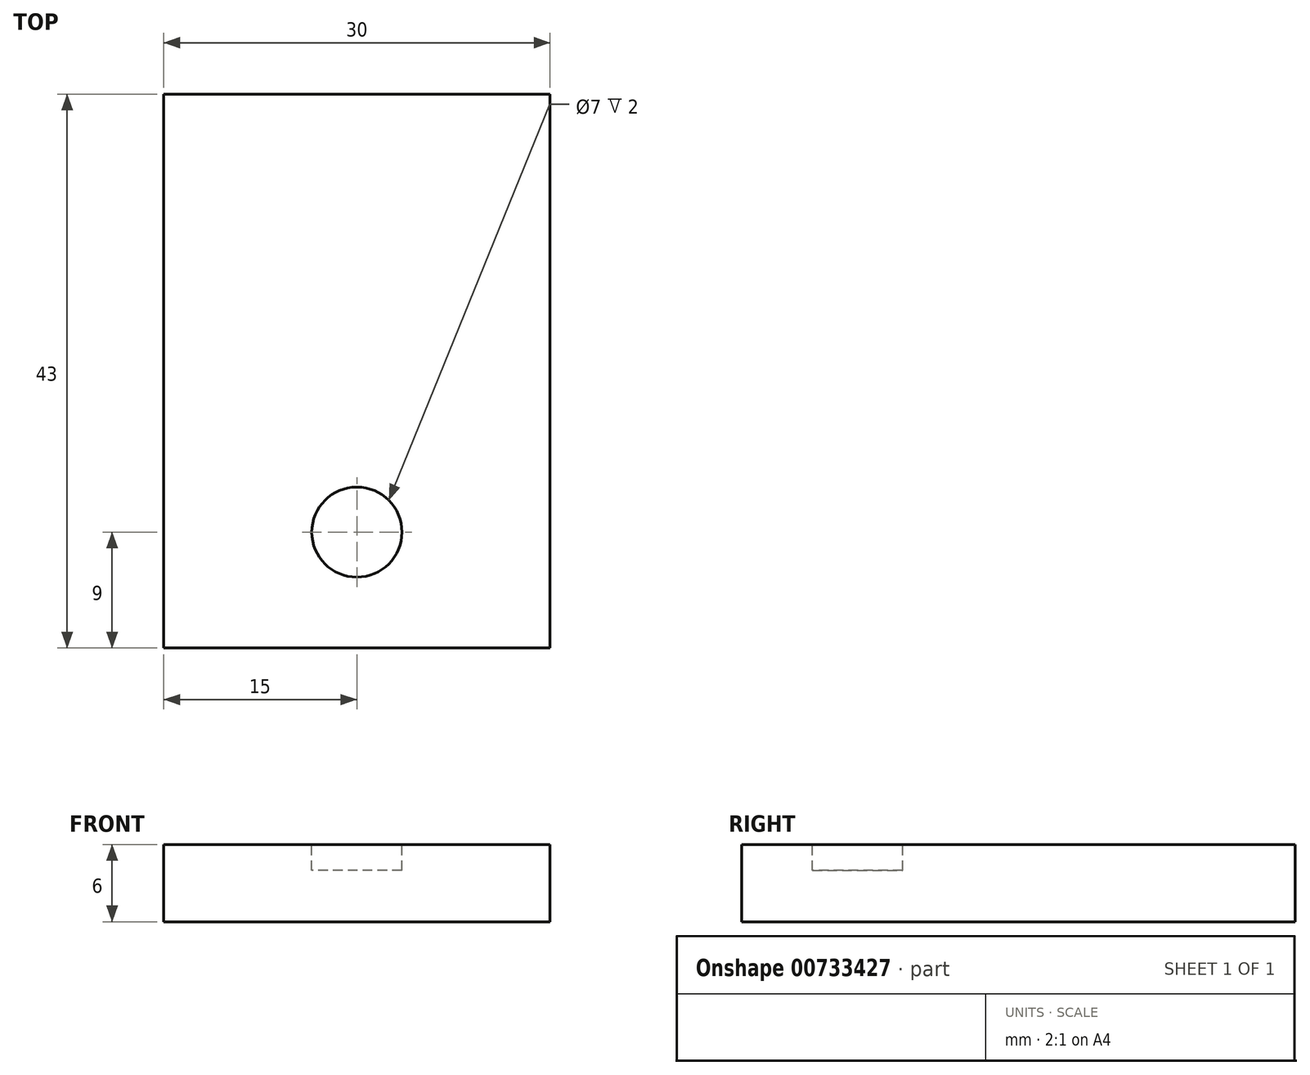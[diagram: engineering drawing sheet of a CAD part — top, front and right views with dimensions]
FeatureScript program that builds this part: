
annotation { "Feature Type Name" : "Feature", "Feature Type Description" : "" }
export const myFeature = defineFeature(function(context is Context, id is Id, definition is map)
    precondition{}
    {
        {
            var Q0;
            Q0=qCreatedBy(makeId("Front.planeOp"),FACE);
            var sketch = newSketch(context, id + "F0", { "sketchPlane" : qUnion([Q0])});
            skLineSegment(sketch, "E0.bottom", {"start": v(15, 3) * mm, "end": v(-15, 3) * mm});
            skLineSegment(sketch, "E0.top", {"start": v(15, -3) * mm, "end": v(-15, -3) * mm});
            skLineSegment(sketch, "E0.left", {"start": v(15, 3) * mm, "end": v(15, -3) * mm});
            skLineSegment(sketch, "E0.right", {"start": v(-15, 3) * mm, "end": v(-15, -3) * mm});
            skPoint(sketch, "E0.middle", {"position": v(0, 0) * mm});
            skSolve(sketch);
        }
        {
            var Q0;
            Q0 = qSketchRegion(id + "F0", true);
            extrude(context, id + "F1", {"entities" : qUnion([Q0]), "depth" : 43 * mm, "offsetDistance" : 25 * mm});
        }
        {
            var Q0;
            Q0=makeQuery(id+"F1.opExtrude","SWEPT_FACE",FACE,{"disambiguationData":[OSD([sQuery(id+"F0.wireOp",EDGE,"E0.bottom")])]});
            var sketch = newSketch(context, id + "F2", { "sketchPlane" : qUnion([Q0])});
            skCircle(sketch, "E1", {"center": v(0, -34) * mm, "radius": 3.5 * mm});
            skSolve(sketch);
        }
        {
            var Q0;
            Q0 = qSketchRegion(id + "F2", true);
            extrude(context, id + "F3", {"entities" : qUnion([Q0]), "operationType" : NewBodyOperationType.REMOVE, "oppositeDirection" : true, "depth" : 2 * mm, "offsetDistance" : 25 * mm});
        }
    });
